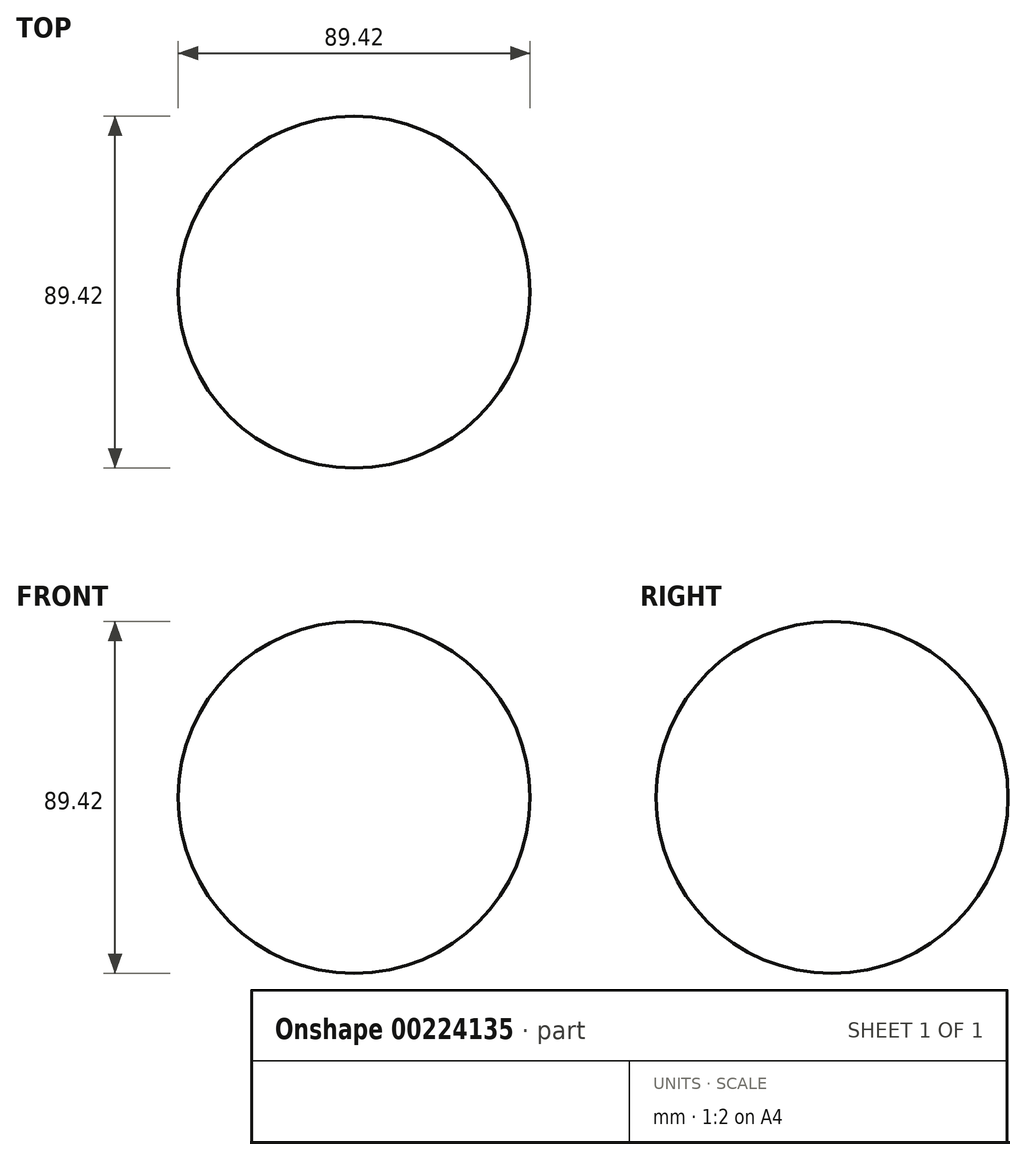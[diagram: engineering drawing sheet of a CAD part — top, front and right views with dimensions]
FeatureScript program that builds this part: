
annotation { "Feature Type Name" : "Feature", "Feature Type Description" : "" }
export const myFeature = defineFeature(function(context is Context, id is Id, definition is map)
    precondition{}
    {
        {
            var Q0;
            Q0=qCreatedBy(makeId("Front.planeOp"),FACE);
            var sketch = newSketch(context, id + "F0", { "sketchPlane" : qUnion([Q0])});
            skCircle(sketch, "E0", {"center": v(0, 0) * mm, "radius": 44.71 * mm});
            skLineSegment(sketch, "E1", {"start": v(0, 44.71) * mm, "end": v(0, -44.71) * mm});
            skSolve(sketch);
        }
        {
            var Q0;
            {var subQ0=sQuery(id+"F0.wireOp",EDGE,"E1");Q0=makeQuery(id+"F0.imprint","IMPRINT",FACE,{"disambiguationData":[TD([[makeQuery(id+"F0.imprint","IMPRINT",EDGE,{"derivedFrom":subQ0}),1.0]])]});}
            var Q1;
            Q1=sQuery(id+"F0.wireOp",EDGE,"E1");
            revolve(context, id + "F1", {"entities" : qUnion([Q0]), "axis" : qUnion([Q1]), "revolveType" : RevolveType.FULL});
        }
    });
